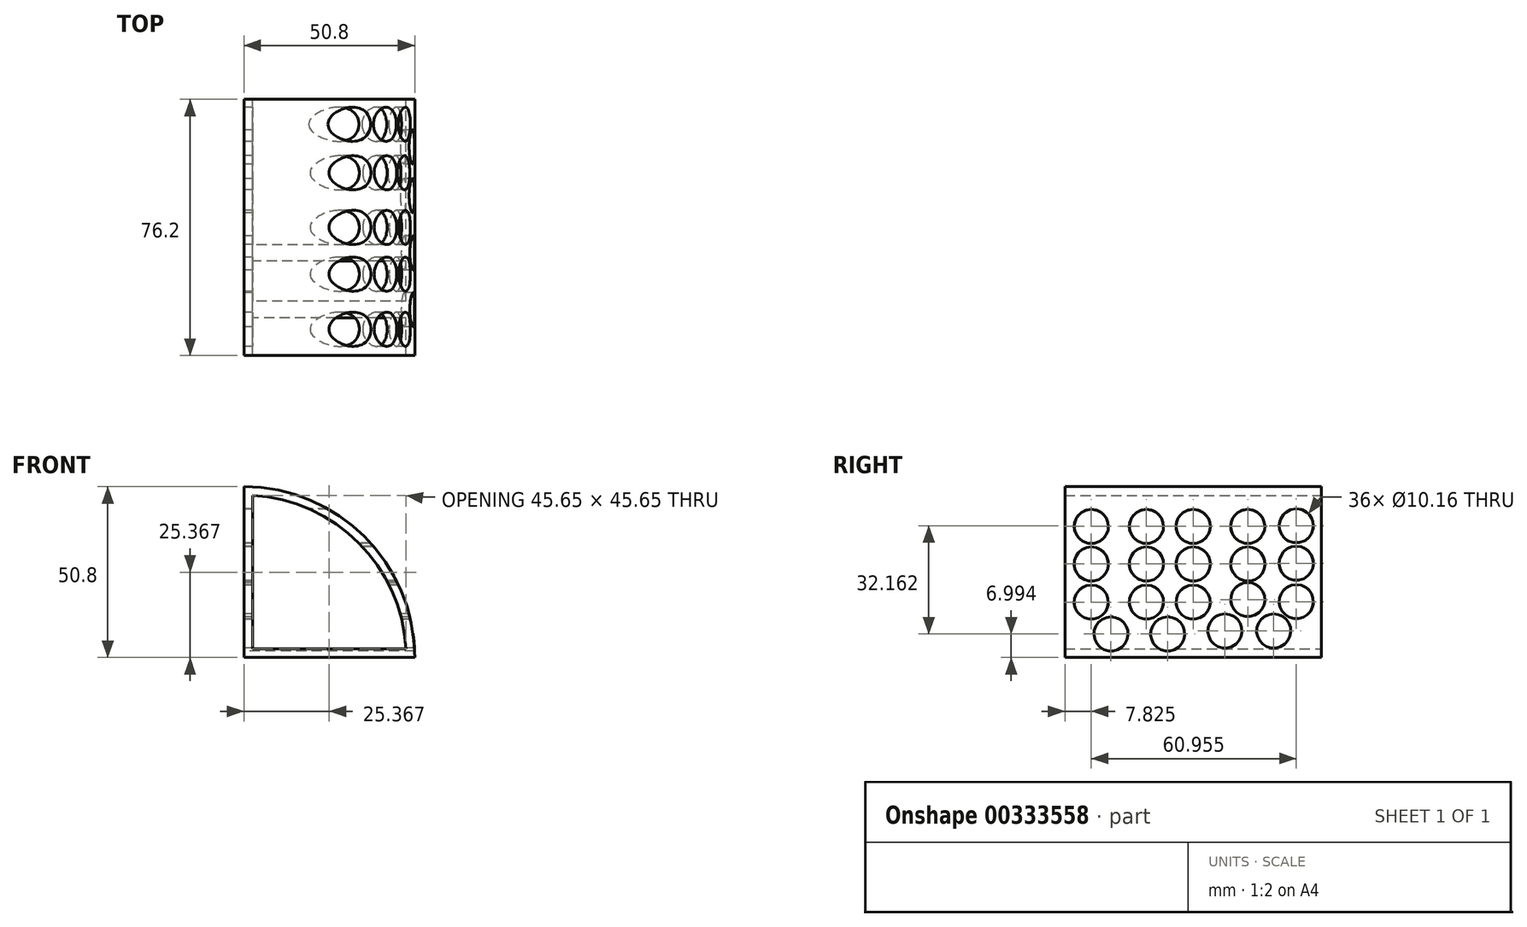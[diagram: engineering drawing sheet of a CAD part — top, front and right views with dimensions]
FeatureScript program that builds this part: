
annotation { "Feature Type Name" : "Feature", "Feature Type Description" : "" }
export const myFeature = defineFeature(function(context is Context, id is Id, definition is map)
    precondition{}
    {
        {
            var Q0;
            Q0=qCreatedBy(makeId("Front.planeOp"),FACE);
            var sketch = newSketch(context, id + "F0", { "sketchPlane" : qUnion([Q0])});
            skLineSegment(sketch, "E0.bottom", {"start": v(0, 0) * mm, "end": v(50.8, 0) * mm});
            skLineSegment(sketch, "E0.left", {"start": v(0, 0) * mm, "end": v(0, 50.8) * mm});
            skArc(sketch, "E1", {"start": v(50.8, 0) * mm, "mid": v(35.92, 35.92) * mm, "end": v(0, 50.8) * mm});
            skSolve(sketch);
        }
        {
            var Q0;
            {var subQ0=sQuery(id+"F0.wireOp",EDGE,"E0.bottom");Q0=makeQuery(id+"F0.imprint","IMPRINT",FACE,{"disambiguationData":[TD([[makeQuery(id+"F0.imprint","IMPRINT",EDGE,{"derivedFrom":subQ0}),1.0]])]});}
            var Q1;
            Q1 = qSketchRegion(id + "F3", true);
            var Q2;
            Q2=sQuery(id+"F0.wireOp",EDGE,"E0.left");
            var Q3;
            Q3=sQuery(id+"F0.wireOp",EDGE,"E0.bottom");
            var Q4;
            Q4=sQuery(id+"F0.wireOp",EDGE,"E1");
            extrude(context, id + "F1", {"entities" : qUnion([Q0, Q1]), "surfaceEntities" : qUnion([Q2, Q3, Q4]), "endBound" : BoundingType.SYMMETRIC, "depth" : 76.2 * mm});
        }
        {
            var Q0;
            Q0=makeQuery(id+"F1.opExtrude","CAP_FACE",FACE,{"disambiguationData":[OSD([sQuery(id+"F0.wireOp",EDGE,"E0.bottom"),sQuery(id+"F0.wireOp",EDGE,"E0.left"),sQuery(id+"F0.wireOp",EDGE,"E1")])],"isStart":false});
            var Q1;
            Q1=makeQuery(id+"F1.opExtrude","CAP_FACE",FACE,{"disambiguationData":[OSD([sQuery(id+"F0.wireOp",EDGE,"E0.bottom"),sQuery(id+"F0.wireOp",EDGE,"E0.left"),sQuery(id+"F0.wireOp",EDGE,"E1")])],"isStart":true});
            shell(context, id + "F2", {"entities" : qUnion([Q0, Q1]), "thickness" : 2.54 * mm});
        }
        {
            var Q0;
            Q0=qCreatedBy(makeId("Right.planeOp"),FACE);
            var sketch = newSketch(context, id + "F3", { "sketchPlane" : qUnion([Q0])});
            skPoint(sketch, "E2", {"position": v(0, 27.8) * mm});
            skPoint(sketch, "E3", {"position": v(-13.89, 27.8) * mm});
            skPoint(sketch, "E4", {"position": v(-13.89, 38.99) * mm});
            skPoint(sketch, "E5", {"position": v(0, 38.99) * mm});
            skPoint(sketch, "E6", {"position": v(16.24, 38.99) * mm});
            skPoint(sketch, "E7", {"position": v(16.24, 27.8) * mm});
            skPoint(sketch, "E8", {"position": v(16.24, 17.24) * mm});
            skPoint(sketch, "E9", {"position": v(0, 16.48) * mm});
            skPoint(sketch, "E10", {"position": v(-13.89, 16.48) * mm});
            skPoint(sketch, "E11", {"position": v(-30.28, 16.48) * mm});
            skPoint(sketch, "E12", {"position": v(-30.28, 27.8) * mm});
            skPoint(sketch, "E13", {"position": v(-30.28, 38.99) * mm});
            skPoint(sketch, "E14", {"position": v(30.68, 39.16) * mm});
            skPoint(sketch, "E15", {"position": v(30.68, 28.04) * mm});
            skPoint(sketch, "E16", {"position": v(30.68, 16.61) * mm});
            skPoint(sketch, "E17", {"position": v(23.95, 7.9) * mm});
            skPoint(sketch, "E18", {"position": v(9.46, 7.9) * mm});
            skPoint(sketch, "E19", {"position": v(-7.56, 7) * mm});
            skPoint(sketch, "E20", {"position": v(-24.44, 7) * mm});
            skSolve(sketch);
        }
        {
            var Q0;
            Q0=sQuery(id+"F3.wireOp",VERTEX,"E14");
            var Q1;
            Q1=sQuery(id+"F3.wireOp",VERTEX,"E6");
            var Q2;
            Q2=sQuery(id+"F3.wireOp",VERTEX,"E5");
            var Q3;
            Q3=sQuery(id+"F3.wireOp",VERTEX,"E4");
            var Q4;
            Q4=sQuery(id+"F3.wireOp",VERTEX,"E13");
            var Q5;
            Q5=sQuery(id+"F3.wireOp",VERTEX,"E12");
            var Q6;
            Q6=sQuery(id+"F3.wireOp",VERTEX,"E3");
            var Q7;
            Q7=sQuery(id+"F3.wireOp",VERTEX,"E7");
            var Q8;
            Q8=sQuery(id+"F3.wireOp",VERTEX,"E15");
            var Q9;
            Q9=sQuery(id+"F3.wireOp",VERTEX,"E16");
            var Q10;
            Q10=sQuery(id+"F3.wireOp",VERTEX,"E8");
            var Q11;
            Q11=sQuery(id+"F3.wireOp",VERTEX,"E9");
            var Q12;
            Q12=sQuery(id+"F3.wireOp",VERTEX,"E2");
            var Q13;
            Q13=sQuery(id+"F3.wireOp",VERTEX,"E10");
            var Q14;
            Q14=sQuery(id+"F3.wireOp",VERTEX,"E11");
            var Q15;
            Q15=sQuery(id+"F3.wireOp",VERTEX,"E17");
            var Q16;
            Q16=sQuery(id+"F3.wireOp",VERTEX,"E18");
            var Q17;
            Q17=sQuery(id+"F3.wireOp",VERTEX,"98a0bfd8-bf74-4be9-8504-e3a85775eec2");
            var Q18;
            Q18=sQuery(id+"F3.wireOp",VERTEX,"E19");
            var Q19;
            Q19=sQuery(id+"F3.wireOp",VERTEX,"E20");
            var Q20;
            Q20=makeQuery(id+"F1.opExtrude","SWEPT_BODY",BODY,{"disambiguationData":[OSD([sQuery(id+"F0.wireOp",EDGE,"E0.bottom"),sQuery(id+"F0.wireOp",EDGE,"E0.left"),sQuery(id+"F0.wireOp",EDGE,"E1")])]});
            hole(context, id + "F4", {"style" : HoleStyle.SIMPLE, "endStyle" : HoleEndStyle.THROUGH, "oppositeDirection" : true, "holeDiameter" : 10.16 * mm, "tappedDepth" : 12.7 * mm, "tapClearance" : 3, "locations" : qUnion([Q0, Q1, Q2, Q3, Q4, Q5, Q6, Q7, Q8, Q9, Q10, Q11, Q12, Q13, Q14, Q15, Q16, Q17, Q18, Q19]), "scope" : qUnion([Q20])});
        }
    });
